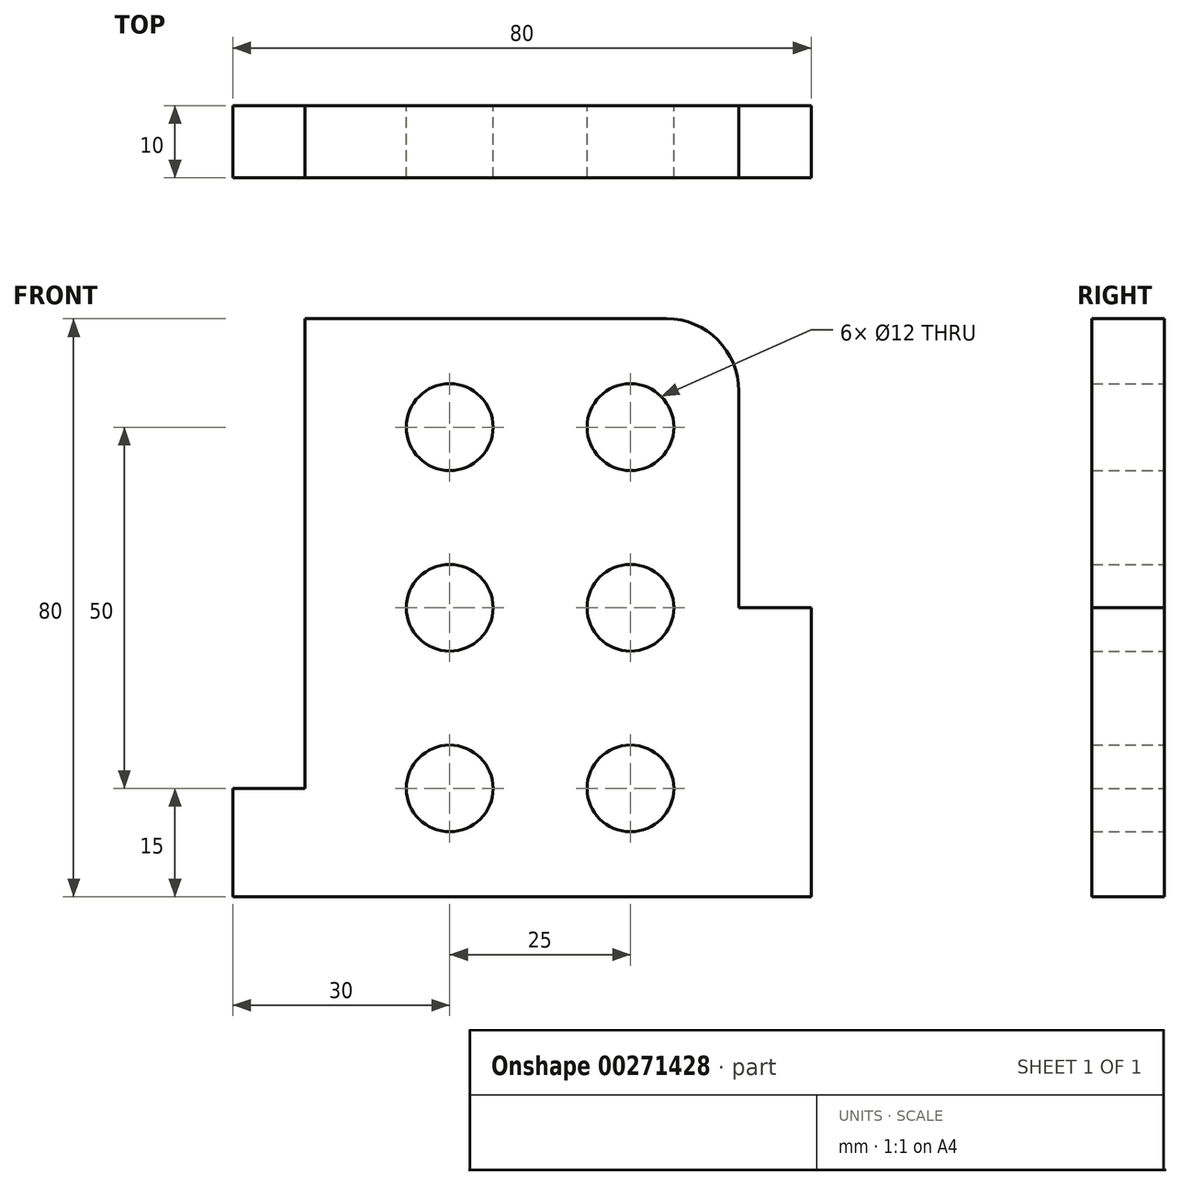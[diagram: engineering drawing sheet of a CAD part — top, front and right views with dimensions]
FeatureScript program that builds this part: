
annotation { "Feature Type Name" : "Feature", "Feature Type Description" : "" }
export const myFeature = defineFeature(function(context is Context, id is Id, definition is map)
    precondition{}
    {
        {
            var Q0;
            Q0=qCreatedBy(makeId("Front.planeOp"),FACE);
            var sketch = newSketch(context, id + "F0", { "sketchPlane" : qUnion([Q0])});
            skLineSegment(sketch, "E0", {"start": v(0, 0) * mm, "end": v(80, 0) * mm});
            skLineSegment(sketch, "E1", {"start": v(80, 0) * mm, "end": v(80, 40) * mm});
            skLineSegment(sketch, "E2", {"start": v(80, 40) * mm, "end": v(70, 40) * mm});
            skLineSegment(sketch, "E3", {"start": v(0, 0) * mm, "end": v(0, 15) * mm});
            skLineSegment(sketch, "E4", {"start": v(0, 15) * mm, "end": v(10, 15) * mm});
            skLineSegment(sketch, "E5", {"start": v(10, 15) * mm, "end": v(10, 80) * mm});
            skLineSegment(sketch, "E6", {"start": v(10, 80) * mm, "end": v(60, 80) * mm});
            skLineSegment(sketch, "E7", {"start": v(70, 40) * mm, "end": v(70, 70) * mm});
            skArc(sketch, "E8", {"start": v(60, 80) * mm, "mid": v(67.07, 77.07) * mm, "end": v(70, 70) * mm});
            skCircle(sketch, "E9", {"center": v(30, 65) * mm, "radius": 6 * mm});
            skCircle(sketch, "E10", {"center": v(55, 65) * mm, "radius": 6 * mm});
            skCircle(sketch, "E11", {"center": v(55, 40) * mm, "radius": 6 * mm});
            skCircle(sketch, "E12", {"center": v(30, 40) * mm, "radius": 6 * mm});
            skCircle(sketch, "E13", {"center": v(30, 15) * mm, "radius": 6 * mm});
            skCircle(sketch, "E14", {"center": v(55, 15) * mm, "radius": 6 * mm});
            skSolve(sketch);
        }
        {
            var Q0;
            Q0 = qSketchRegion(id + "F0", true);
            extrude(context, id + "F1", {"entities" : qUnion([Q0]), "depth" : 10 * mm});
        }
    });
